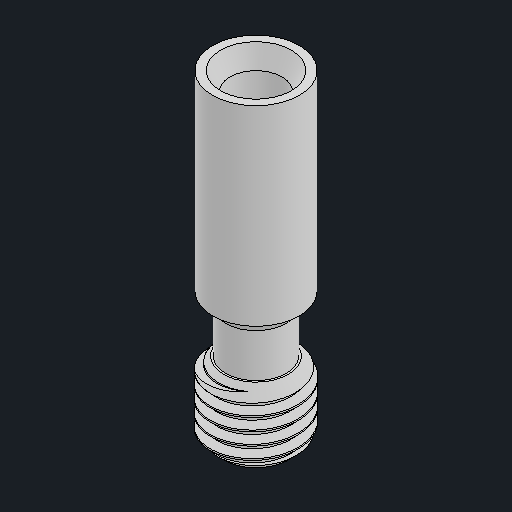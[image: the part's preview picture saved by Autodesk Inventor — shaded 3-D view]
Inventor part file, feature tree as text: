
AUTODESK INVENTOR PART (.ipt)
format: ipt  version: 2024.2 (Build 282272000, 272)  size: 245,248 bytes
history: native  units: mm
features: other x1, chamfer x1
ambient origin geometry x8: Origin, YZ Plane, XZ Plane, XY Plane, X Axis, Y Axis, Z Axis, Center Point
bodies: Body1 (feature_tree)
feature tree (2):
  other  "솔리드1"
  chamfer  "Chamfer2"  [1 undecoded]
note: 1 required parameter value undecoded (feature->parameter linkage not recoverable at this tier; creation-order binding heuristic only, values carry confidence <= 0.55)
